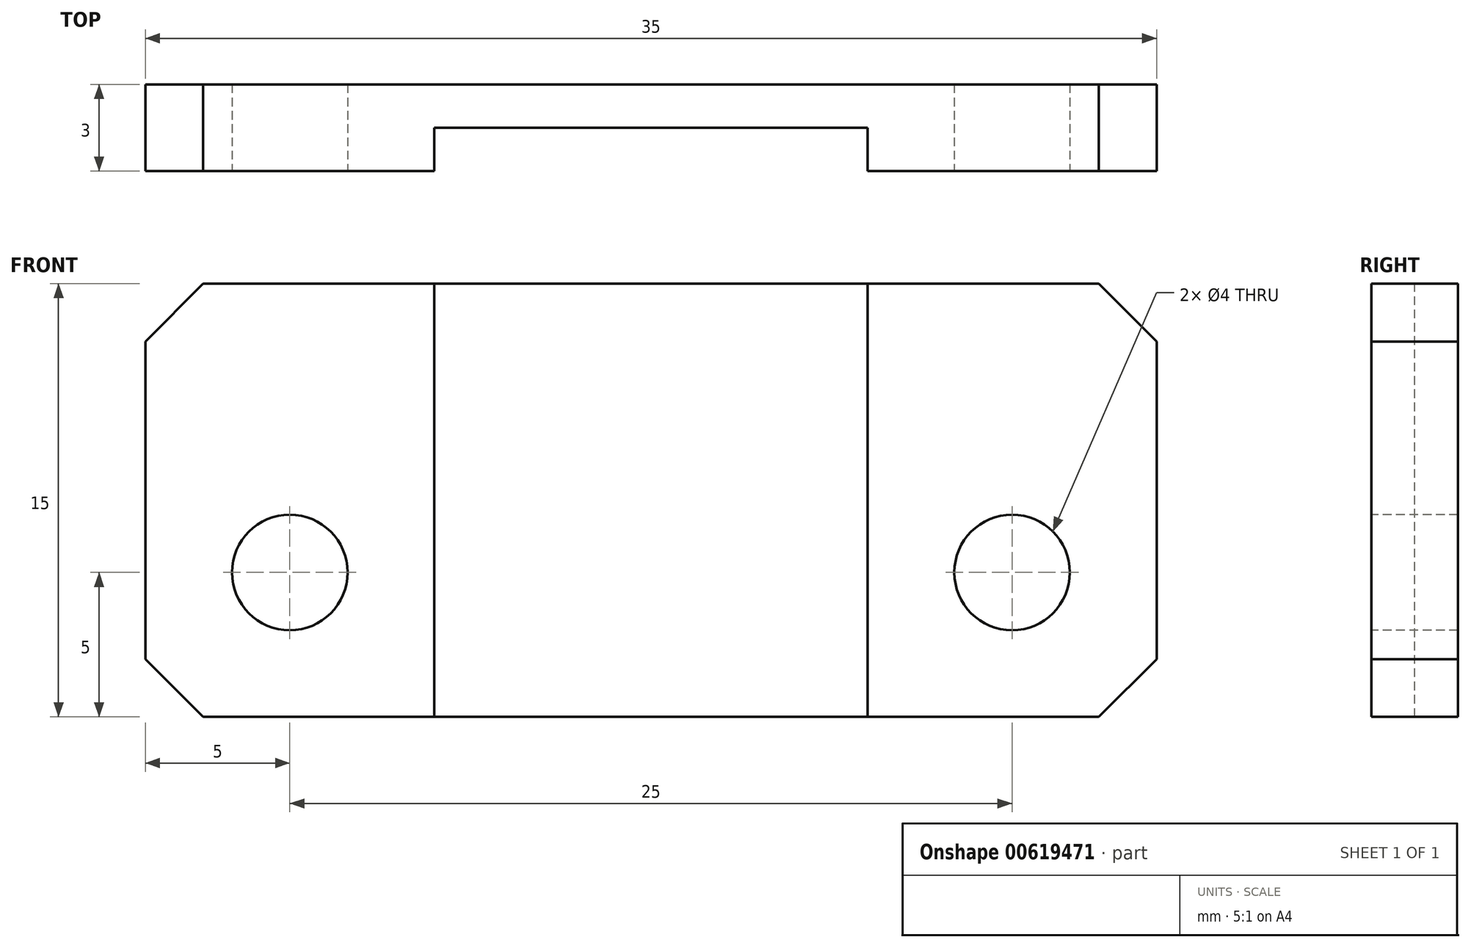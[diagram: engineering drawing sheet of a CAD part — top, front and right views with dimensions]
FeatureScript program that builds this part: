
annotation { "Feature Type Name" : "Feature", "Feature Type Description" : "" }
export const myFeature = defineFeature(function(context is Context, id is Id, definition is map)
    precondition{}
    {
        {
            var Q0;
            Q0=qCreatedBy(makeId("Front.planeOp"),FACE);
            var sketch = newSketch(context, id + "F0", { "sketchPlane" : qUnion([Q0])});
            skLineSegment(sketch, "E0.bottom", {"start": v(-17.5, 7.5) * mm, "end": v(17.5, 7.5) * mm});
            skLineSegment(sketch, "E0.top", {"start": v(-17.5, -7.5) * mm, "end": v(17.5, -7.5) * mm});
            skLineSegment(sketch, "E0.left", {"start": v(-17.5, 7.5) * mm, "end": v(-17.5, -7.5) * mm});
            skLineSegment(sketch, "E0.right", {"start": v(17.5, 7.5) * mm, "end": v(17.5, -7.5) * mm});
            skPoint(sketch, "E0.middle", {"position": v(0, 0) * mm});
            skSolve(sketch);
        }
        {
            var Q0;
            Q0=makeQuery(id+"F0.imprint","IMPRINT",FACE,{"disambiguationData":[TD([[makeQuery(id+"F0.imprint","IMPRINT",EDGE,{"derivedFrom":sQuery(id+"F0.wireOp",EDGE,"E0.bottom")}),-1.0]])]});
            extrude(context, id + "F1", {"entities" : qUnion([Q0]), "depth" : 4.5 * mm, "offsetDistance" : 25 * mm});
        }
        {
            var Q0;
            Q0=makeQuery(id+"F1.opExtrude","SWEPT_FACE",FACE,{"disambiguationData":[OSD([sQuery(id+"F0.wireOp",EDGE,"E0.bottom")])]});
            var sketch = newSketch(context, id + "F2", { "sketchPlane" : qUnion([Q0])});
            skLineSegment(sketch, "E1.bottom", {"start": v(-7.5, -1.5) * mm, "end": v(7.5, -1.5) * mm});
            skLineSegment(sketch, "E1.top", {"start": v(-7.5, -3) * mm, "end": v(7.5, -3) * mm});
            skLineSegment(sketch, "E1.left", {"start": v(-7.5, -1.5) * mm, "end": v(-7.5, -3) * mm});
            skLineSegment(sketch, "E1.right", {"start": v(7.5, -1.5) * mm, "end": v(7.5, -3) * mm});
            skPoint(sketch, "E1.middle", {"position": v(0, -2.25) * mm});
            skPoint(sketch, "E1.middle.positionSnap0", {"position": v(17.5, -2.25) * mm});
            skPoint(sketch, "E1.centerSnap0", {"position": v(17.5, -2.25) * mm});
            skSolve(sketch);
        }
        {
            var Q0;
            Q0=qSketchRegion(id+"F2",true);
            extrude(context, id + "F3", {"entities" : qUnion([Q0]), "operationType" : NewBodyOperationType.REMOVE, "endBound" : BoundingType.THROUGH_ALL, "oppositeDirection" : true, "depth" : 25 * mm, "offsetDistance" : 25 * mm});
        }
        {
            var Q0;
            Q0=makeQuery(id+"F1.opExtrude","CAP_FACE",FACE,{"disambiguationData":[OSD([sQuery(id+"F0.wireOp",EDGE,"E0.bottom"),sQuery(id+"F0.wireOp",EDGE,"E0.top"),sQuery(id+"F0.wireOp",EDGE,"E0.left"),sQuery(id+"F0.wireOp",EDGE,"E0.right")])],"isStart":false});
            var sketch = newSketch(context, id + "F4", { "sketchPlane" : qUnion([Q0])});
            skCircle(sketch, "E2", {"center": v(12.5, -2.5) * mm, "radius": 2 * mm});
            skCircle(sketch, "E3.MirrorC", {"center": v(-12.5, -2.5) * mm, "radius": 2 * mm});
            skSolve(sketch);
        }
        {
            var Q0;
            Q0=qSketchRegion(id+"F4",true);
            extrude(context, id + "F5", {"entities" : qUnion([Q0]), "operationType" : NewBodyOperationType.REMOVE, "oppositeDirection" : true, "depth" : 10 * mm, "offsetDistance" : 25 * mm});
        }
        {
            var Q0;
            Q0=makeQuery(id+"F1.opExtrude","SWEPT_EDGE",EDGE,{"disambiguationData":[OSD([sQuery(id+"F0.wireOp",EDGE,"E0.bottom"),sQuery(id+"F0.wireOp",EDGE,"E0.left")])]});
            var Q1;
            Q1=makeQuery(id+"F1.opExtrude","SWEPT_EDGE",EDGE,{"disambiguationData":[OSD([sQuery(id+"F0.wireOp",EDGE,"E0.bottom"),sQuery(id+"F0.wireOp",EDGE,"E0.right")])]});
            var Q2;
            Q2=makeQuery(id+"F1.opExtrude","SWEPT_EDGE",EDGE,{"disambiguationData":[OSD([sQuery(id+"F0.wireOp",EDGE,"E0.top"),sQuery(id+"F0.wireOp",EDGE,"E0.right")])]});
            var Q3;
            Q3=makeQuery(id+"F1.opExtrude","SWEPT_EDGE",EDGE,{"disambiguationData":[OSD([sQuery(id+"F0.wireOp",EDGE,"E0.top"),sQuery(id+"F0.wireOp",EDGE,"E0.left")])]});
            chamfer(context, id + "F6", {"entities" : qUnion([Q0, Q1, Q2, Q3]), "width" : 2 * mm, "tangentPropagation" : true});
        }
        {
            var Q0;
            Q0=makeQuery(id+"F1.opExtrude","SWEPT_FACE",FACE,{"disambiguationData":[OSD([sQuery(id+"F0.wireOp",EDGE,"E0.bottom")])]});
            var sketch = newSketch(context, id + "F7", { "sketchPlane" : qUnion([Q0])});
            skLineSegment(sketch, "E4.bottom", {"start": v(-19.05, -4.5) * mm, "end": v(20.2, -4.5) * mm});
            skLineSegment(sketch, "E4.top", {"start": v(-19.05, -3) * mm, "end": v(20.2, -3) * mm});
            skLineSegment(sketch, "E4.left", {"start": v(-19.05, -4.5) * mm, "end": v(-19.05, -3) * mm});
            skLineSegment(sketch, "E4.right", {"start": v(20.2, -4.5) * mm, "end": v(20.2, -3) * mm});
            skSolve(sketch);
        }
        {
            var Q0;
            Q0 = qSketchRegion(id + "F7", true);
            extrude(context, id + "F8", {"entities" : qUnion([Q0]), "operationType" : NewBodyOperationType.REMOVE, "endBound" : BoundingType.THROUGH_ALL, "oppositeDirection" : true, "depth" : 25 * mm, "offsetDistance" : 25 * mm});
        }
    });
